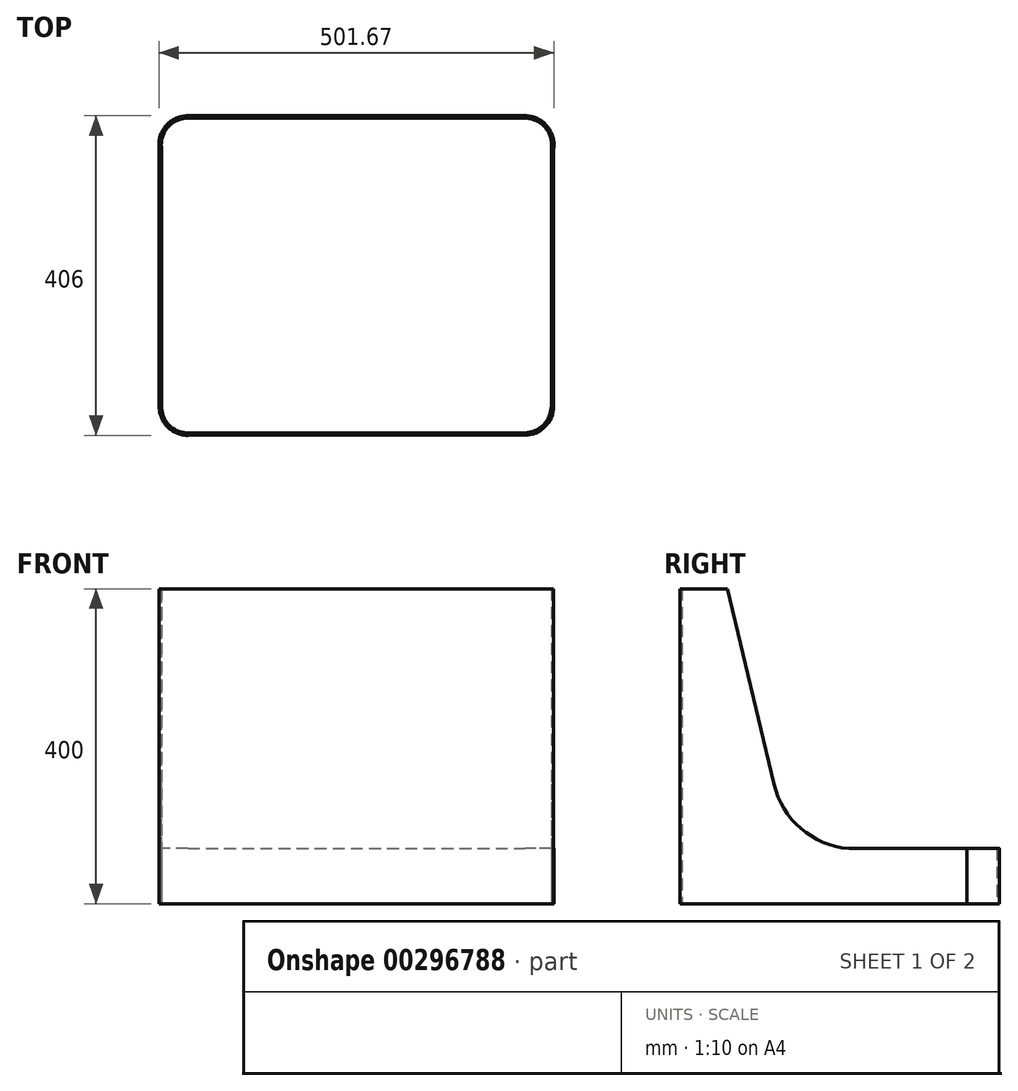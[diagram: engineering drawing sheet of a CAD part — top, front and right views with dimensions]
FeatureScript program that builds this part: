
annotation { "Feature Type Name" : "Feature", "Feature Type Description" : "" }
export const myFeature = defineFeature(function(context is Context, id is Id, definition is map)
    precondition{}
    {
        {
            var Q0;
            Q0=qCreatedBy(makeId("Top.planeOp"),FACE);
            var sketch = newSketch(context, id + "F0", { "sketchPlane" : qUnion([Q0])});
            skPoint(sketch, "E0.visualSharp", {"position": v(-247.97, 203.35) * mm});
            skArc(sketch, "E0.filletArc", {"start": v(-213.31, 208.06) * mm, "mid": v(-238.9, 196.62) * mm, "end": v(-246.91, 169.75) * mm});
            skPoint(sketch, "E1.visualSharp", {"position": v(247.03, 203.35) * mm});
            skArc(sketch, "E1.filletArc", {"start": v(248.09, 169.75) * mm, "mid": v(240.08, 196.62) * mm, "end": v(214.49, 208.06) * mm});
            skPoint(sketch, "E2.visualSharp", {"position": v(247.03, -191.65) * mm});
            skArc(sketch, "E2.filletArc", {"start": v(214.5, -191.65) * mm, "mid": v(238.25, -181.8) * mm, "end": v(248.09, -158.05) * mm});
            skArc(sketch, "E3.filletArc", {"start": v(-246.91, -158.34) * mm, "mid": v(-237.07, -182.1) * mm, "end": v(-213.3, -191.94) * mm});
            skLineSegment(sketch, "E4", {"start": v(248.09, 169.75) * mm, "end": v(248.09, -158.05) * mm});
            skLineSegment(sketch, "E5", {"start": v(214.5, -191.65) * mm, "end": v(-213.3, -191.94) * mm});
            skLineSegment(sketch, "E6", {"start": v(-246.91, -158.34) * mm, "end": v(-246.91, 169.75) * mm});
            skLineSegment(sketch, "E7", {"start": v(-213.31, 208.06) * mm, "end": v(214.49, 208.06) * mm});
            skLineSegment(sketch, "E8.0", {"start": v(-213.3, 211.06) * mm, "end": v(214.47, 211.06) * mm});
            skArc(sketch, "E8.1", {"start": v(251.09, 169.54) * mm, "mid": v(242.27, 198.67) * mm, "end": v(214.47, 211.06) * mm});
            skArc(sketch, "E8.2", {"start": v(-213.3, 211.06) * mm, "mid": v(-241.1, 198.67) * mm, "end": v(-249.91, 169.54) * mm});
            skLineSegment(sketch, "E8.3", {"start": v(251.09, 169.54) * mm, "end": v(251.09, -158.05) * mm});
            skLineSegment(sketch, "E8.4", {"start": v(-249.91, -158.34) * mm, "end": v(-249.91, 169.54) * mm});
            skArc(sketch, "E8.5", {"start": v(-249.91, -158.34) * mm, "mid": v(-239.19, -184.23) * mm, "end": v(-213.29, -194.94) * mm});
            skLineSegment(sketch, "E8.6", {"start": v(214.51, -194.65) * mm, "end": v(-213.29, -194.94) * mm});
            skArc(sketch, "E8.7", {"start": v(214.51, -194.65) * mm, "mid": v(240.37, -183.92) * mm, "end": v(251.09, -158.05) * mm});
            skSolve(sketch);
        }
        {
            var Q0;
            Q0=makeQuery(id+"F0.imprint","IMPRINT",FACE,{"disambiguationData":[TD([[makeQuery(id+"F0.imprint","IMPRINT",EDGE,{"derivedFrom":sQuery(id+"F0.wireOp",EDGE,"E0.filletArc")}),-1.0]])]});
            var Q1;
            Q1=sQuery(id+"F0.wireOp",EDGE,"E8.4");
            var Q2;
            Q2=sQuery(id+"F0.wireOp",EDGE,"E8.5");
            var Q3;
            Q3=sQuery(id+"F0.wireOp",EDGE,"E8.6");
            var Q4;
            Q4=sQuery(id+"F0.wireOp",EDGE,"E8.7");
            var Q5;
            Q5=sQuery(id+"F0.wireOp",EDGE,"E8.3");
            var Q6;
            Q6=sQuery(id+"F0.wireOp",EDGE,"E8.2");
            var Q7;
            Q7=sQuery(id+"F0.wireOp",EDGE,"E8.0");
            var Q8;
            Q8=sQuery(id+"F0.wireOp",EDGE,"E8.1");
            extrude(context, id + "F1", {"entities" : qUnion([Q0]), "surfaceEntities" : qUnion([Q1, Q2, Q3, Q4, Q5, Q6, Q7, Q8]), "depth" : 400 * mm});
        }
        {
            var Q0;
            Q0=makeQuery(id+"F1.opExtrude","SWEPT_FACE",FACE,{"disambiguationData":[OSD([sQuery(id+"F0.wireOp",EDGE,"E8.3")])]});
            var sketch = newSketch(context, id + "F2", { "sketchPlane" : qUnion([Q0])});
            skLineSegment(sketch, "E9", {"start": v(-134.61, 400) * mm, "end": v(-75.47, 152.05) * mm});
            skLineSegment(sketch, "E10", {"start": v(19.54, 70) * mm, "end": v(169.54, 70) * mm});
            skArc(sketch, "E11", {"start": v(-75.47, 152.05) * mm, "mid": v(-41.2, 95.7) * mm, "end": v(19.54, 70) * mm});
            skSolve(sketch);
        }
        {
            var Q0;
            {var subQ5=sQuery(id+"F2.wireOp",EDGE,"E9");Q0=makeQuery(id+"F2.imprint","IMPRINT",FACE,{"disambiguationData":[TD([[makeQuery(id+"F2.imprint","IMPRINT",EDGE,{"derivedFrom":subQ5}),1.0]])]});}
            extrude(context, id + "F3", {"entities" : qUnion([Q0]), "operationType" : NewBodyOperationType.REMOVE, "oppositeDirection" : true, "depth" : 550 * mm});
        }
        {
            var Q0;
            {var subQ0=sQuery(id+"F0.wireOp",EDGE,"E4");var subQ1=sQuery(id+"F0.wireOp",EDGE,"E6");var subQ2=sQuery(id+"F0.wireOp",EDGE,"E1.filletArc");var subQ3=sQuery(id+"F0.wireOp",EDGE,"E8.0");var subQ4=sQuery(id+"F0.wireOp",EDGE,"E0.filletArc");var subQ5=sQuery(id+"F0.wireOp",EDGE,"E7");var subQ6=sQuery(id+"F0.wireOp",EDGE,"E8.1");var subQ7=sQuery(id+"F0.wireOp",EDGE,"E8.4");var subQ8=sQuery(id+"F0.wireOp",EDGE,"E8.2");var subQ9=sQuery(id+"F0.wireOp",EDGE,"E8.3");Q0=makeQuery(id+"F3.boolean.opBoolean","SPLIT",FACE,{"disambiguationData":[TD([makeQuery(id+"F1.opExtrude","SWEPT_FACE",FACE,{"disambiguationData":[OSD([subQ4])]})])],"derivedFrom":makeQuery(id+"F1.opExtrude","CAP_FACE",FACE,{"disambiguationData":[OSD([subQ4,subQ2,sQuery(id+"F0.wireOp",EDGE,"E2.filletArc"),sQuery(id+"F0.wireOp",EDGE,"E3.filletArc"),subQ0,sQuery(id+"F0.wireOp",EDGE,"E5"),subQ1,subQ5,subQ3,subQ6,subQ8,subQ9,subQ7,sQuery(id+"F0.wireOp",EDGE,"E8.5"),sQuery(id+"F0.wireOp",EDGE,"E8.6"),sQuery(id+"F0.wireOp",EDGE,"E8.7")])],"isStart":false})});}
            extrude(context, id + "F4", {"entities" : qUnion([Q0]), "operationType" : NewBodyOperationType.REMOVE, "oppositeDirection" : true, "depth" : 330 * mm});
        }
    });
